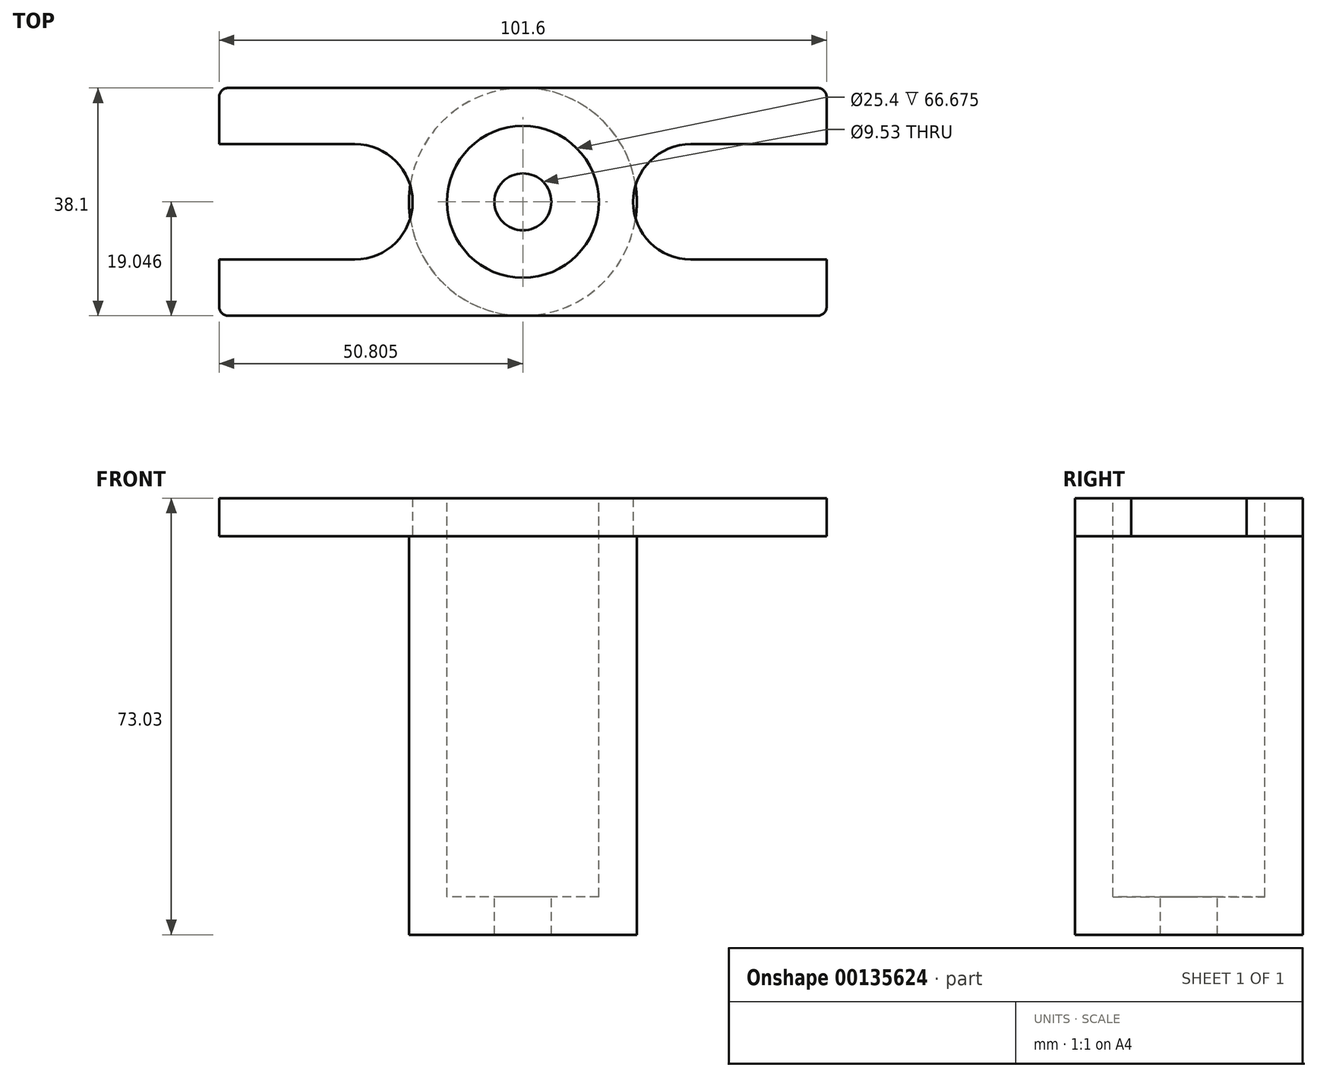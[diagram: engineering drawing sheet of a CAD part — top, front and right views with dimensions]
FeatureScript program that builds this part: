
annotation { "Feature Type Name" : "Feature", "Feature Type Description" : "" }
export const myFeature = defineFeature(function(context is Context, id is Id, definition is map)
    precondition{}
    {
        {
            var Q0;
            Q0=qCreatedBy(makeId("Top.planeOp"),FACE);
            var sketch = newSketch(context, id + "F0", { "sketchPlane" : qUnion([Q0])});
            skLineSegment(sketch, "E0", {"start": v(-48.84, 29.48) * mm, "end": v(52.76, 29.48) * mm});
            skLineSegment(sketch, "E1", {"start": v(52.76, 29.48) * mm, "end": v(52.76, 20.08) * mm});
            skLineSegment(sketch, "E2", {"start": v(-48.84, 29.48) * mm, "end": v(-48.84, 20.08) * mm});
            skLineSegment(sketch, "E3", {"start": v(-48.84, 20.08) * mm, "end": v(-26.13, 20.08) * mm});
            skLineSegment(sketch, "E4", {"start": v(52.76, 20.08) * mm, "end": v(30.06, 20.08) * mm});
            skArc(sketch, "E5", {"start": v(-26.13, 0.77) * mm, "mid": v(-16.47, 10.43) * mm, "end": v(-26.13, 20.08) * mm});
            skArc(sketch, "E6", {"start": v(30.06, 20.08) * mm, "mid": v(20.4, 10.43) * mm, "end": v(30.06, 0.77) * mm});
            skLineSegment(sketch, "E7", {"start": v(-26.13, 0.77) * mm, "end": v(-48.84, 0.77) * mm});
            skLineSegment(sketch, "E8", {"start": v(-48.84, 0.77) * mm, "end": v(-48.84, -8.62) * mm});
            skLineSegment(sketch, "E9", {"start": v(-48.84, -8.62) * mm, "end": v(52.76, -8.62) * mm});
            skLineSegment(sketch, "E10", {"start": v(52.76, -8.62) * mm, "end": v(52.76, 0.77) * mm});
            skLineSegment(sketch, "E11", {"start": v(52.76, 0.77) * mm, "end": v(30.06, 0.77) * mm});
            skSolve(sketch);
        }
        {
            var Q0;
            Q0 = qSketchRegion(id + "F0", true);
            extrude(context, id + "F1", {"entities" : qUnion([Q0]), "endBound" : BoundingType.SYMMETRIC, "depth" : 6.35 * mm});
        }
        {
            var Q0;
            Q0=makeQuery(id+"F1.opExtrude","SWEPT_EDGE",EDGE,{"disambiguationData":[OSD([sQuery(id+"F0.wireOp",EDGE,"E0"),sQuery(id+"F0.wireOp",EDGE,"E1")])]});
            var Q1;
            Q1=makeQuery(id+"F1.opExtrude","SWEPT_EDGE",EDGE,{"disambiguationData":[OSD([sQuery(id+"F0.wireOp",EDGE,"E9"),sQuery(id+"F0.wireOp",EDGE,"E10")])]});
            var Q2;
            Q2=makeQuery(id+"F1.opExtrude","SWEPT_EDGE",EDGE,{"disambiguationData":[OSD([sQuery(id+"F0.wireOp",EDGE,"E8"),sQuery(id+"F0.wireOp",EDGE,"E9")])]});
            var Q3;
            Q3=makeQuery(id+"F1.opExtrude","SWEPT_EDGE",EDGE,{"disambiguationData":[OSD([sQuery(id+"F0.wireOp",EDGE,"E0"),sQuery(id+"F0.wireOp",EDGE,"E2")])]});
            fillet(context, id + "F2", {"entities" : qUnion([Q0, Q1, Q2, Q3]), "radius" : 1.52 * mm, "tangentPropagation" : true, "allowEdgeOverflow" : false});
        }
        {
            var Q0;
            Q0=qCreatedBy(makeId("Top.planeOp"),FACE);
            var sketch = newSketch(context, id + "F3", { "sketchPlane" : qUnion([Q0])});
            skCircle(sketch, "E12", {"center": v(1.96, 10.43) * mm, "radius": 12.7 * mm});
            skArc(sketch, "E13.0", {"start": v(-26.13, 0.77) * mm, "mid": v(-16.47, 10.43) * mm, "end": v(-26.13, 20.08) * mm});
            skSolve(sketch);
        }
        {
            var Q0;
            Q0=qCreatedBy(makeId("Top.planeOp"),FACE);
            var sketch = newSketch(context, id + "F4", { "sketchPlane" : qUnion([Q0])});
            skCircle(sketch, "E14", {"center": v(1.96, 10.43) * mm, "radius": 19.05 * mm});
            skSolve(sketch);
        }
        {
            var Q0;
            Q0 = qSketchRegion(id + "F4", true);
            var Q1;
            Q1=makeQuery(id+"F1.opExtrude","CAP_FACE",FACE,{"disambiguationData":[OSD([sQuery(id+"F0.wireOp",EDGE,"E0"),sQuery(id+"F0.wireOp",EDGE,"E1"),sQuery(id+"F0.wireOp",EDGE,"E2"),sQuery(id+"F0.wireOp",EDGE,"E3"),sQuery(id+"F0.wireOp",EDGE,"E4"),sQuery(id+"F0.wireOp",EDGE,"E5"),sQuery(id+"F0.wireOp",EDGE,"E6"),sQuery(id+"F0.wireOp",EDGE,"E7"),sQuery(id+"F0.wireOp",EDGE,"E8"),sQuery(id+"F0.wireOp",EDGE,"E9"),sQuery(id+"F0.wireOp",EDGE,"E10"),sQuery(id+"F0.wireOp",EDGE,"E11")])],"isStart":true});
            extrude(context, id + "F5", {"entities" : qUnion([Q0]), "operationType" : NewBodyOperationType.ADD, "oppositeDirection" : true, "depth" : 69.85 * mm, "hasSecondDirection" : true, "secondDirectionBound" : SecondDirectionBoundingType.UP_TO_SURFACE, "secondDirectionOppositeDirection" : true, "secondDirectionBoundEntityFace" : qUnion([Q1]), "secondDirectionDepth" : 25.4 * mm});
        }
        {
            var Q0;
            Q0 = qSketchRegion(id + "F3", true);
            extrude(context, id + "F6", {"entities" : qUnion([Q0]), "operationType" : NewBodyOperationType.REMOVE, "oppositeDirection" : true, "depth" : 63.5 * mm, "hasSecondDirection" : true, "secondDirectionOppositeDirection" : false, "secondDirectionDepth" : 25.4 * mm});
        }
        {
            var Q0;
            Q0=qCreatedBy(makeId("Top.planeOp"),FACE);
            var sketch = newSketch(context, id + "F7", { "sketchPlane" : qUnion([Q0])});
            skCircle(sketch, "E15", {"center": v(1.96, 10.43) * mm, "radius": 4.76 * mm});
            skSolve(sketch);
        }
        {
            var Q0;
            Q0 = qSketchRegion(id + "F7", true);
            extrude(context, id + "F8", {"entities" : qUnion([Q0]), "operationType" : NewBodyOperationType.REMOVE, "oppositeDirection" : true, "depth" : 75.1 * mm});
        }
    });
